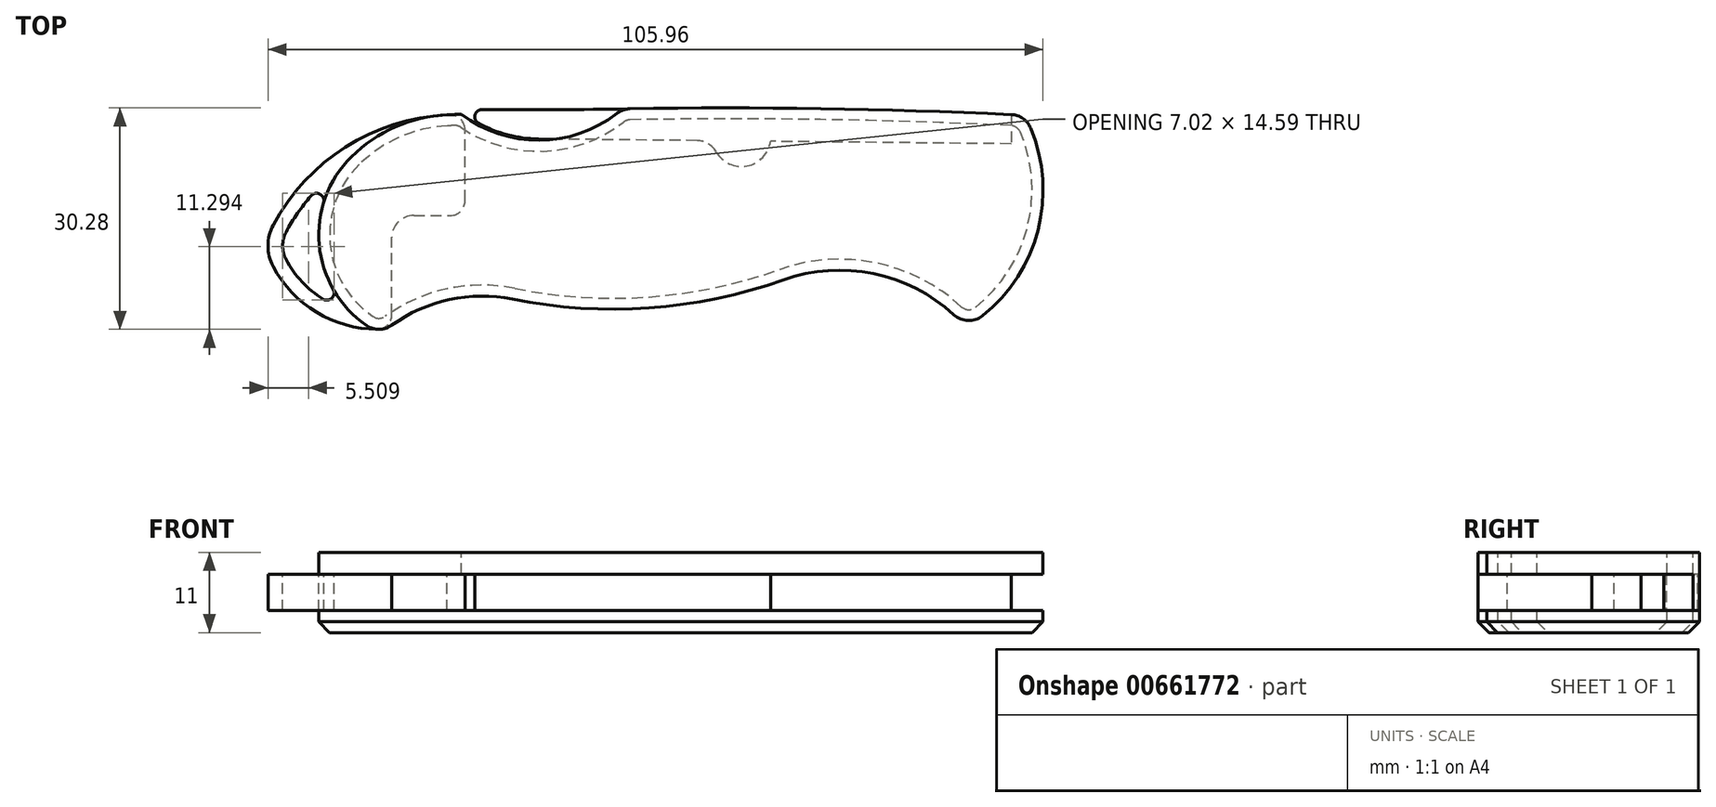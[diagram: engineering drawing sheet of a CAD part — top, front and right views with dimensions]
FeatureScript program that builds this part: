
annotation { "Feature Type Name" : "Feature", "Feature Type Description" : "" }
export const myFeature = defineFeature(function(context is Context, id is Id, definition is map)
    precondition{}
    {
        {
            var Q0;
            Q0=qCreatedBy(makeId("Top.planeOp"),FACE);
            var sketch = newSketch(context, id + "F0", { "sketchPlane" : qUnion([Q0])});
            skLineSegment(sketch, "E0", {"start": v(-50, 0) * mm, "end": v(50, 0) * mm, "construction": true});
            skLineSegment(sketch, "E1", {"start": v(-50, 15) * mm, "end": v(48, 15) * mm});
            skLineSegment(sketch, "E2", {"start": v(48, 15) * mm, "end": v(40, -14) * mm, "construction": true});
            skLineSegment(sketch, "E3", {"start": v(-50, 15) * mm, "end": v(-50, -15) * mm});
            skArc(sketch, "E4", {"start": v(40, -14) * mm, "mid": v(49.73, -1.08) * mm, "end": v(48, 15) * mm});
            skLineSegment(sketch, "E5", {"start": v(-50, -15) * mm, "end": v(40, -14) * mm});
            skSolve(sketch);
        }
        {
            var Q0;
            Q0 = qSketchRegion(id + "F0", true);
            extrude(context, id + "F1", {"entities" : qUnion([Q0]), "depth" : 3 * mm, "offsetDistance" : 25 * mm});
        }
        {
            var Q0;
            Q0=makeQuery(id+"F1.opExtrude","CAP_FACE",FACE,{"disambiguationData":[OSD([sQuery(id+"F0.wireOp",EDGE,"E1"),sQuery(id+"F0.wireOp",EDGE,"E3"),sQuery(id+"F0.wireOp",EDGE,"i1TKLzg2-nzSs-Z2fB-SjIf-EBck5CtR53aa"),sQuery(id+"F0.wireOp",EDGE,"E4")])],"isStart":false});
            var sketch = newSketch(context, id + "F2", { "sketchPlane" : qUnion([Q0])});
            skLineSegment(sketch, "E6", {"start": v(-40, -14.89) * mm, "end": v(40, -14) * mm});
            skArc(sketch, "E7", {"start": v(-22, -10.15) * mm, "mid": v(-31.55, -10.43) * mm, "end": v(-40, -14.89) * mm});
            skArc(sketch, "E8", {"start": v(-22, -10.15) * mm, "mid": v(-3.33, -11.36) * mm, "end": v(15, -7.52) * mm});
            skArc(sketch, "E9", {"start": v(40, -14) * mm, "mid": v(28.49, -6.93) * mm, "end": v(15, -7.52) * mm});
            skSolve(sketch);
        }
        {
            var Q0;
            Q0 = qSketchRegion(id + "F2", true);
            extrude(context, id + "F3", {"entities" : qUnion([Q0]), "operationType" : NewBodyOperationType.REMOVE, "endBound" : BoundingType.THROUGH_ALL, "oppositeDirection" : true, "depth" : 25 * mm, "offsetDistance" : 25 * mm});
        }
        {
            var Q0;
            Q0=makeQuery(id+"F1.opExtrude","CAP_FACE",FACE,{"disambiguationData":[OSD([sQuery(id+"F0.wireOp",EDGE,"E1"),sQuery(id+"F0.wireOp",EDGE,"E3"),sQuery(id+"F0.wireOp",EDGE,"E4"),sQuery(id+"F0.wireOp",EDGE,"E5")])],"isStart":false});
            var sketch = newSketch(context, id + "F4", { "sketchPlane" : qUnion([Q0])});
            skArc(sketch, "E10", {"start": v(48, 15) * mm, "mid": v(8, 16) * mm, "end": v(-32, 15) * mm});
            skLineSegment(sketch, "E11", {"start": v(-32, 15) * mm, "end": v(48, 15) * mm});
            skSolve(sketch);
        }
        {
            var Q0;
            Q0 = qSketchRegion(id + "F4", true);
            var Q1;
            Q1=makeQuery(id+"F1.opExtrude","CAP_FACE",FACE,{"disambiguationData":[OSD([sQuery(id+"F0.wireOp",EDGE,"E1"),sQuery(id+"F0.wireOp",EDGE,"E3"),sQuery(id+"F0.wireOp",EDGE,"E4"),sQuery(id+"F0.wireOp",EDGE,"E5")])],"isStart":true});
            extrude(context, id + "F5", {"entities" : qUnion([Q0]), "operationType" : NewBodyOperationType.ADD, "endBound" : BoundingType.UP_TO_SURFACE, "oppositeDirection" : true, "depth" : 25 * mm, "endBoundEntityFace" : qUnion([Q1]), "offsetDistance" : 25 * mm});
        }
        {
            var Q0;
            Q0=makeQuery(id+"F5.boolean.opBoolean","MERGE",FACE,{"derivedFrom":[makeQuery(id+"F1.opExtrude","CAP_FACE",FACE,{"disambiguationData":[OSD([sQuery(id+"F0.wireOp",EDGE,"E1"),sQuery(id+"F0.wireOp",EDGE,"E3"),sQuery(id+"F0.wireOp",EDGE,"E4"),sQuery(id+"F0.wireOp",EDGE,"E5")])],"isStart":false}),makeQuery(id+"F5.opExtrude","CAP_FACE",FACE,{"disambiguationData":[OSD([sQuery(id+"F4.wireOp",EDGE,"E10"),sQuery(id+"F4.wireOp",EDGE,"E11")])],"isStart":true})]});
            var sketch = newSketch(context, id + "F6", { "sketchPlane" : qUnion([Q0])});
            skArc(sketch, "E12", {"start": v(-29, 15.14) * mm, "mid": v(-17.87, 11.58) * mm, "end": v(-7, 15.86) * mm});
            skArc(sketch, "E13.0", {"start": v(-7, 15.86) * mm, "mid": v(-18, 15.58) * mm, "end": v(-29, 15.14) * mm});
            skPoint(sketch, "E14.orphan", {"position": v(-32, 15) * mm});
            skPoint(sketch, "E15.orphan", {"position": v(48, 15) * mm});
            skSolve(sketch);
        }
        {
            var Q0;
            Q0 = qSketchRegion(id + "F6", true);
            extrude(context, id + "F7", {"entities" : qUnion([Q0]), "operationType" : NewBodyOperationType.REMOVE, "endBound" : BoundingType.THROUGH_ALL, "oppositeDirection" : true, "depth" : 25 * mm, "offsetDistance" : 25 * mm});
        }
        {
            var Q0;
            Q0=makeQuery(id+"F1.opExtrude","SWEPT_EDGE",EDGE,{"disambiguationData":[OSD([sQuery(id+"F0.wireOp",EDGE,"E1"),sQuery(id+"F0.wireOp",EDGE,"E3")])]});
            fillet(context, id + "F8", {"entities" : qUnion([Q0]), "radius" : 20 * mm, "tangentPropagation" : true, "allowEdgeOverflow" : false});
        }
        {
            var Q0;
            Q0=makeQuery(id+"F1.opExtrude","SWEPT_EDGE",EDGE,{"disambiguationData":[OSD([sQuery(id+"F0.wireOp",EDGE,"E3"),sQuery(id+"F0.wireOp",EDGE,"E5")])]});
            fillet(context, id + "F9", {"entities" : qUnion([Q0]), "radius" : 15 * mm, "tangentPropagation" : true, "allowEdgeOverflow" : false});
        }
        {
            var Q0;
            {var subQ0=sQuery(id+"F0.wireOp",EDGE,"E4");Q0=makeQuery(id+"F5.boolean.opBoolean","MERGE",EDGE,{"derivedFrom":[makeQuery(id+"F1.opExtrude","SWEPT_EDGE",EDGE,{"disambiguationData":[OSD([sQuery(id+"F0.wireOp",EDGE,"E1"),subQ0])]}),makeQuery(id+"F5.opExtrude","SWEPT_EDGE",EDGE,{"disambiguationData":[OSD([subQ0,sQuery(id+"F4.wireOp",EDGE,"E10"),sQuery(id+"F4.wireOp",EDGE,"E11")])]})]});}
            var Q1;
            {var subQ0=sQuery(id+"F0.wireOp",EDGE,"E4");Q1=makeQuery(id+"F3.boolean.opBoolean","MERGE",EDGE,{"derivedFrom":[makeQuery(id+"F1.opExtrude","SWEPT_EDGE",EDGE,{"disambiguationData":[OSD([subQ0,sQuery(id+"F0.wireOp",EDGE,"E5")])]}),makeQuery(id+"F3.opExtrude","SWEPT_EDGE",EDGE,{"disambiguationData":[OSD([subQ0,sQuery(id+"F2.wireOp",EDGE,"E6"),sQuery(id+"F2.wireOp",EDGE,"E9")])]})]});}
            var Q2;
            Q2=makeQuery(id+"F9.opFillet","BLEND_EDGE",EDGE,{"blendedFrom":[makeQuery(id+"F1.opExtrude","SWEPT_EDGE",EDGE,{"disambiguationData":[OSD([sQuery(id+"F0.wireOp",EDGE,"E3"),sQuery(id+"F0.wireOp",EDGE,"E5")])]}),makeQuery(id+"F3.boolean.opBoolean","COPY",FACE,{"derivedFrom":makeQuery(id+"F3.opExtrude","SWEPT_FACE",FACE,{"disambiguationData":[OSD([sQuery(id+"F2.wireOp",EDGE,"E7")])]})})],"blendedInto":[makeQuery(id+"F3.boolean.opBoolean","COPY",FACE,{"derivedFrom":makeQuery(id+"F3.opExtrude","SWEPT_FACE",FACE,{"disambiguationData":[OSD([sQuery(id+"F2.wireOp",EDGE,"E7")])]})})]});
            var Q3;
            {var subQ0=sQuery(id+"F6.wireOp",EDGE,"E13.0");var subQ1=sQuery(id+"F6.wireOp",EDGE,"E12");var subQ2=sQuery(id+"F4.wireOp",EDGE,"E10");Q3=makeQuery(id+"F7.boolean.opBoolean","COPY",EDGE,{"derivedFrom":makeQuery(id+"F7.opExtrude","SWEPT_EDGE",EDGE,{"disambiguationData":[OSD([subQ2,subQ1,subQ0]),TDD([makeQuery(id+"F6.imprint","INTERSECT",VERTEX,{"disambiguationData":[OD(0.0)],"derivedFrom":[makeQuery(id+"F5.opExtrude","CAP_EDGE",EDGE,{"disambiguationData":[OSD([subQ2])],"isStart":true}),subQ1,subQ0]})])]})});}
            var Q4;
            {var subQ0=sQuery(id+"F6.wireOp",EDGE,"E13.0");var subQ1=sQuery(id+"F6.wireOp",EDGE,"E12");var subQ2=sQuery(id+"F4.wireOp",EDGE,"E10");Q4=makeQuery(id+"F7.boolean.opBoolean","COPY",EDGE,{"derivedFrom":makeQuery(id+"F7.opExtrude","SWEPT_EDGE",EDGE,{"disambiguationData":[OSD([subQ2,subQ1,subQ0]),TDD([makeQuery(id+"F6.imprint","INTERSECT",VERTEX,{"disambiguationData":[OD(1.0)],"derivedFrom":[makeQuery(id+"F5.opExtrude","CAP_EDGE",EDGE,{"disambiguationData":[OSD([subQ2])],"isStart":true}),subQ1,subQ0]})])]})});}
            fillet(context, id + "F10", {"entities" : qUnion([Q0, Q1, Q2, Q3, Q4]), "radius" : 3 * mm, "tangentPropagation" : true, "allowEdgeOverflow" : false});
        }
        {
            var Q0;
            Q0=makeQuery(id+"F5.boolean.opBoolean","MERGE",FACE,{"derivedFrom":[makeQuery(id+"F1.opExtrude","CAP_FACE",FACE,{"disambiguationData":[OSD([sQuery(id+"F0.wireOp",EDGE,"E1"),sQuery(id+"F0.wireOp",EDGE,"E3"),sQuery(id+"F0.wireOp",EDGE,"E4"),sQuery(id+"F0.wireOp",EDGE,"E5")])],"isStart":true}),makeQuery(id+"F5.opExtrude","CAP_FACE",FACE,{"disambiguationData":[OSD([sQuery(id+"F4.wireOp",EDGE,"E10"),sQuery(id+"F4.wireOp",EDGE,"E11")])],"isStart":false})]});
            var sketch = newSketch(context, id + "F11", { "sketchPlane" : qUnion([Q0])});
            skLineSegment(sketch, "E16", {"start": v(-38.52, 13.72) * mm, "end": v(-38.52, -1.28) * mm});
            skLineSegment(sketch, "E17", {"start": v(-38.52, -1.28) * mm, "end": v(-28.52, -1.28) * mm});
            skLineSegment(sketch, "E18", {"start": v(-28.52, -1.28) * mm, "end": v(-28.52, -15.05) * mm});
            skArc(sketch, "E19", {"start": v(-38.52, 13.72) * mm, "mid": v(-39.33, 14.13) * mm, "end": v(-40.23, 14.28) * mm});
            skArc(sketch, "E20", {"start": v(-40.23, 14.28) * mm, "mid": v(-48.7, 12.02) * mm, "end": v(-54.74, 5.67) * mm});
            skArc(sketch, "E21", {"start": v(-54.74, 5.67) * mm, "mid": v(-55.44, 2.87) * mm, "end": v(-54.74, 0.06) * mm});
            skArc(sketch, "E22", {"start": v(-54.74, 0.06) * mm, "mid": v(-44.86, -10.64) * mm, "end": v(-30.97, -15.05) * mm});
            skLineSegment(sketch, "E23", {"start": v(-30.97, -15.05) * mm, "end": v(-28.52, -15.05) * mm});
            skSolve(sketch);
        }
        {
            var Q0;
            Q0 = qSketchRegion(id + "F11", true);
            extrude(context, id + "F12", {"entities" : qUnion([Q0]), "depth" : 5 * mm, "offsetDistance" : 25 * mm});
        }
        {
            var Q0;
            Q0=makeQuery(id+"F12.opExtrude","CAP_FACE",FACE,{"disambiguationData":[OSD([sQuery(id+"F11.wireOp",EDGE,"E16"),sQuery(id+"F11.wireOp",EDGE,"E17"),sQuery(id+"F11.wireOp",EDGE,"E18"),sQuery(id+"F11.wireOp",EDGE,"E19"),sQuery(id+"F11.wireOp",EDGE,"E20"),sQuery(id+"F11.wireOp",EDGE,"E21"),sQuery(id+"F11.wireOp",EDGE,"E22")])],"isStart":true});
            var sketch = newSketch(context, id + "F13", { "sketchPlane" : qUnion([Q0])});
            skArc(sketch, "E24.0", {"start": v(-44.35, -11.73) * mm, "mid": v(-48.5, -2.08) * mm, "end": v(-45.29, 7.93) * mm});
            skArc(sketch, "E25.0", {"start": v(-52.98, -1) * mm, "mid": v(-49.63, 3.9) * mm, "end": v(-45.29, 7.93) * mm});
            skArc(sketch, "E25.1", {"start": v(-52.98, -4.74) * mm, "mid": v(-53.44, -2.87) * mm, "end": v(-52.98, -1) * mm});
            skArc(sketch, "E25.2", {"start": v(-44.35, -11.73) * mm, "mid": v(-49.38, -9.11) * mm, "end": v(-52.98, -4.74) * mm});
            skPoint(sketch, "E26.orphan", {"position": v(-41.96, -13.76) * mm});
            skPoint(sketch, "E27.orphan", {"position": v(-30.97, 15.05) * mm});
            skPoint(sketch, "E28.orphan", {"position": v(-44.04, 9.31) * mm});
            skSolve(sketch);
        }
        {
            var Q0;
            Q0 = qSketchRegion(id + "F13", true);
            extrude(context, id + "F14", {"entities" : qUnion([Q0]), "operationType" : NewBodyOperationType.REMOVE, "endBound" : BoundingType.THROUGH_ALL, "oppositeDirection" : true, "depth" : 25 * mm, "offsetDistance" : 25 * mm});
        }
        {
            var Q0;
            Q0=makeQuery(id+"F14.boolean.opBoolean","COPY",EDGE,{"derivedFrom":makeQuery(id+"F14.opExtrude","SWEPT_EDGE",EDGE,{"disambiguationData":[OSD([sQuery(id+"F13.wireOp",EDGE,"E24.0"),sQuery(id+"F13.wireOp",EDGE,"E25.0")])]})});
            var Q1;
            Q1=makeQuery(id+"F14.boolean.opBoolean","COPY",EDGE,{"derivedFrom":makeQuery(id+"F14.opExtrude","SWEPT_EDGE",EDGE,{"disambiguationData":[OSD([sQuery(id+"F13.wireOp",EDGE,"E24.0"),sQuery(id+"F13.wireOp",EDGE,"E25.2")])]})});
            fillet(context, id + "F15", {"entities" : qUnion([Q0, Q1]), "radius" : 1 * mm, "tangentPropagation" : true, "allowEdgeOverflow" : false});
        }
        {
            var Q0;
            Q0=makeQuery(id+"F12.opExtrude","SWEPT_EDGE",EDGE,{"disambiguationData":[OSD([sQuery(id+"F11.wireOp",EDGE,"E18"),sQuery(id+"F11.wireOp",EDGE,"E22")])]});
            var Q1;
            Q1=makeQuery(id+"F12.opExtrude","SWEPT_EDGE",EDGE,{"disambiguationData":[OSD([sQuery(id+"F11.wireOp",EDGE,"E17"),sQuery(id+"F11.wireOp",EDGE,"E18")])]});
            var Q2;
            Q2=makeQuery(id+"F12.opExtrude","SWEPT_EDGE",EDGE,{"disambiguationData":[OSD([sQuery(id+"F0.wireOp",EDGE,"E1"),sQuery(id+"F0.wireOp",EDGE,"E3"),sQuery(id+"F0.wireOp",EDGE,"E4"),sQuery(id+"F0.wireOp",EDGE,"E5"),sQuery(id+"F2.wireOp",EDGE,"E7"),sQuery(id+"F11.wireOp",EDGE,"E16"),sQuery(id+"F11.wireOp",EDGE,"E19")])]});
            fillet(context, id + "F16", {"entities" : qUnion([Q0, Q1, Q2]), "radius" : 2 * mm, "tangentPropagation" : true, "allowEdgeOverflow" : false});
        }
        {
            var Q0;
            Q0=makeQuery(id+"F12.opExtrude","SWEPT_EDGE",EDGE,{"disambiguationData":[OSD([sQuery(id+"F11.wireOp",EDGE,"E16"),sQuery(id+"F11.wireOp",EDGE,"E17")])]});
            fillet(context, id + "F17", {"entities" : qUnion([Q0]), "radius" : 3 * mm, "tangentPropagation" : true, "allowEdgeOverflow" : false});
        }
        {
            var Q0;
            Q0=makeQuery(id+"F5.boolean.opBoolean","MERGE",FACE,{"derivedFrom":[makeQuery(id+"F1.opExtrude","CAP_FACE",FACE,{"disambiguationData":[OSD([sQuery(id+"F0.wireOp",EDGE,"E1"),sQuery(id+"F0.wireOp",EDGE,"E3"),sQuery(id+"F0.wireOp",EDGE,"E4"),sQuery(id+"F0.wireOp",EDGE,"E5")])],"isStart":true}),makeQuery(id+"F5.opExtrude","CAP_FACE",FACE,{"disambiguationData":[OSD([sQuery(id+"F4.wireOp",EDGE,"E10"),sQuery(id+"F4.wireOp",EDGE,"E11")])],"isStart":false})]});
            var sketch = newSketch(context, id + "F18", { "sketchPlane" : qUnion([Q0])});
            skArc(sketch, "E29.0", {"start": v(-5.95, -15.88) * mm, "mid": v(20.13, -15.9) * mm, "end": v(46.2, -15.09) * mm});
            skArc(sketch, "E30", {"start": v(-29.45, -15.81) * mm, "mid": v(-17.7, -15.76) * mm, "end": v(-5.95, -15.88) * mm});
            skArc(sketch, "E31", {"start": v(-18.47, -11.76) * mm, "mid": v(-24.31, -12.83) * mm, "end": v(-29.45, -15.81) * mm});
            skLineSegment(sketch, "E32", {"start": v(46.2, -15.09) * mm, "end": v(46.16, -11.09) * mm});
            skLineSegment(sketch, "E33", {"start": v(46.16, -11.09) * mm, "end": v(-18.47, -11.76) * mm});
            skSolve(sketch);
        }
        {
            var Q0;
            Q0 = qSketchRegion(id + "F18", true);
            var Q1;
            Q1=makeQuery(id+"F12.opExtrude","CAP_FACE",FACE,{"disambiguationData":[OSD([sQuery(id+"F11.wireOp",EDGE,"E16"),sQuery(id+"F11.wireOp",EDGE,"E17"),sQuery(id+"F11.wireOp",EDGE,"E18"),sQuery(id+"F11.wireOp",EDGE,"E19"),sQuery(id+"F11.wireOp",EDGE,"E20"),sQuery(id+"F11.wireOp",EDGE,"E21"),sQuery(id+"F11.wireOp",EDGE,"E22"),sQuery(id+"F11.wireOp",EDGE,"E23")])],"isStart":false});
            extrude(context, id + "F19", {"entities" : qUnion([Q0]), "endBound" : BoundingType.UP_TO_SURFACE, "depth" : 25 * mm, "endBoundEntityFace" : qUnion([Q1]), "offsetDistance" : 25 * mm});
        }
        {
            var Q0;
            Q0=makeQuery(id+"F19.opExtrude","CAP_FACE",FACE,{"disambiguationData":[OSD([sQuery(id+"F18.wireOp",EDGE,"E29.0"),sQuery(id+"F18.wireOp",EDGE,"E30"),sQuery(id+"F18.wireOp",EDGE,"E31"),sQuery(id+"F18.wireOp",EDGE,"E32"),sQuery(id+"F18.wireOp",EDGE,"E33")])],"isStart":false});
            var sketch = newSketch(context, id + "F20", { "sketchPlane" : qUnion([Q0])});
            skPoint(sketch, "E34", {"position": v(9.3, -12) * mm});
            skLineSegment(sketch, "E35", {"start": v(9.3, -12) * mm, "end": v(49.3, -12) * mm, "construction": true});
            skCircle(sketch, "E36", {"center": v(9.3, -12) * mm, "radius": 2 * mm, "construction": true});
            skCircle(sketch, "E37.0", {"center": v(9.3, -12) * mm, "radius": 4 * mm, "construction": true});
            skLineSegment(sketch, "E38", {"start": v(9.3, -8) * mm, "end": v(9.3, 11.36) * mm, "construction": true});
            skArc(sketch, "E39", {"start": v(13.26, -11.43) * mm, "mid": v(9.26, -8) * mm, "end": v(5.33, -11.51) * mm});
            skLineSegment(sketch, "E40", {"start": v(5.33, -11.51) * mm, "end": v(13.26, -11.43) * mm});
            skSolve(sketch);
        }
        {
            var Q0;
            Q0 = qSketchRegion(id + "F20", true);
            extrude(context, id + "F21", {"entities" : qUnion([Q0]), "operationType" : NewBodyOperationType.ADD, "oppositeDirection" : true, "depth" : 5 * mm, "offsetDistance" : 25 * mm});
        }
        {
            var Q0;
            {var subQ0=sQuery(id+"F20.wireOp",EDGE,"E40");var subQ1=sQuery(id+"F20.wireOp",EDGE,"E39");var subQ2=sQuery(id+"F18.wireOp",EDGE,"E33");Q0=makeQuery(id+"F21.opExtrude","SWEPT_EDGE",EDGE,{"disambiguationData":[OSD([subQ2,subQ1,subQ0]),TDD([makeQuery(id+"F20.imprint","INTERSECT",VERTEX,{"disambiguationData":[OD(1.0)],"derivedFrom":[makeQuery(id+"F19.opExtrude","CAP_EDGE",EDGE,{"disambiguationData":[OSD([subQ2])],"isStart":false}),subQ1,subQ0]})])]});}
            var Q1;
            {var subQ0=sQuery(id+"F20.wireOp",EDGE,"E40");var subQ1=sQuery(id+"F20.wireOp",EDGE,"E39");var subQ2=sQuery(id+"F18.wireOp",EDGE,"E33");Q1=makeQuery(id+"F21.opExtrude","SWEPT_EDGE",EDGE,{"disambiguationData":[OSD([subQ2,subQ1,subQ0]),TDD([makeQuery(id+"F20.imprint","INTERSECT",VERTEX,{"disambiguationData":[OD(0.0)],"derivedFrom":[makeQuery(id+"F19.opExtrude","CAP_EDGE",EDGE,{"disambiguationData":[OSD([subQ2])],"isStart":false}),subQ1,subQ0]})])]});}
            fillet(context, id + "F22", {"entities" : qUnion([Q0, Q1]), "radius" : 3 * mm, "tangentPropagation" : true, "allowEdgeOverflow" : false});
        }
        {
            var Q0;
            Q0=makeQuery(id+"F19.opExtrude","SWEPT_EDGE",EDGE,{"disambiguationData":[OSD([sQuery(id+"F18.wireOp",EDGE,"E30"),sQuery(id+"F18.wireOp",EDGE,"E31")])]});
            fillet(context, id + "F23", {"entities" : qUnion([Q0]), "radius" : 1 * mm, "tangentPropagation" : true, "allowEdgeOverflow" : false});
        }
        {
            var Q0;
            Q0=makeQuery(id+"F12.opExtrude","CAP_FACE",FACE,{"disambiguationData":[OSD([sQuery(id+"F11.wireOp",EDGE,"E16"),sQuery(id+"F11.wireOp",EDGE,"E17"),sQuery(id+"F11.wireOp",EDGE,"E18"),sQuery(id+"F11.wireOp",EDGE,"E19"),sQuery(id+"F11.wireOp",EDGE,"E20"),sQuery(id+"F11.wireOp",EDGE,"E21"),sQuery(id+"F11.wireOp",EDGE,"E22")])],"isStart":false});
            var sketch = newSketch(context, id + "F24", { "sketchPlane" : qUnion([Q0])});
            skArc(sketch, "E41.0.0", {"start": v(-30.97, -15.05) * mm, "mid": v(-30.5, -15.07) * mm, "end": v(-30.05, -15.1) * mm});
            skArc(sketch, "E41.0.1", {"start": v(-30.05, -15.1) * mm, "mid": v(-29.09, -14.99) * mm, "end": v(-28.22, -14.58) * mm});
            skArc(sketch, "E41.0.2", {"start": v(-28.22, -14.58) * mm, "mid": v(-17.87, -11.58) * mm, "end": v(-7.74, -15.25) * mm});
            skArc(sketch, "E41.0.3", {"start": v(-7.74, -15.25) * mm, "mid": v(-6.9, -15.7) * mm, "end": v(-5.95, -15.88) * mm});
            skArc(sketch, "E41.0.4", {"start": v(-5.95, -15.88) * mm, "mid": v(20.13, -15.9) * mm, "end": v(46.2, -15.09) * mm});
            skArc(sketch, "E41.0.5", {"start": v(46.2, -15.09) * mm, "mid": v(47.78, -14.55) * mm, "end": v(48.82, -13.25) * mm});
            skArc(sketch, "E41.0.6", {"start": v(48.82, -13.25) * mm, "mid": v(49.83, 0.7) * mm, "end": v(42.23, 12.44) * mm});
            skArc(sketch, "E41.0.7", {"start": v(42.23, 12.44) * mm, "mid": v(40.25, 13.09) * mm, "end": v(38.33, 12.3) * mm});
            skArc(sketch, "E41.0.8", {"start": v(38.33, 12.3) * mm, "mid": v(27.33, 6.66) * mm, "end": v(15, 7.52) * mm});
            skArc(sketch, "E41.0.9", {"start": v(15, 7.52) * mm, "mid": v(-3.33, 11.36) * mm, "end": v(-22, 10.15) * mm});
            skArc(sketch, "E41.0.10", {"start": v(-22, 10.15) * mm, "mid": v(-30.63, 10.21) * mm, "end": v(-38.52, 13.72) * mm});
            skArc(sketch, "E41.0.11", {"start": v(-38.52, 13.72) * mm, "mid": v(-40.23, 14.28) * mm, "end": v(-41.96, 13.76) * mm});
            skArc(sketch, "E41.0.12", {"start": v(-41.96, 13.76) * mm, "mid": v(-48.45, 2.71) * mm, "end": v(-44.04, -9.31) * mm});
            skArc(sketch, "E41.0.13", {"start": v(-44.04, -9.31) * mm, "mid": v(-38.04, -13.39) * mm, "end": v(-30.97, -15.05) * mm});
            skSolve(sketch);
        }
        {
            var Q0;
            Q0 = qSketchRegion(id + "F24", true);
            extrude(context, id + "F25", {"entities" : qUnion([Q0]), "depth" : 3 * mm, "offsetDistance" : 25 * mm});
        }
        {
            var Q0;
            Q0=makeQuery(id+"F3.boolean.opBoolean","COPY",EDGE,{"derivedFrom":makeQuery(id+"F3.opExtrude","CAP_EDGE",EDGE,{"disambiguationData":[OSD([sQuery(id+"F2.wireOp",EDGE,"E8")])],"isStart":true})});
            var Q1;
            Q1=makeQuery(id+"F25.opExtrude","CAP_EDGE",EDGE,{"disambiguationData":[OSD([sQuery(id+"F24.wireOp",EDGE,"E41.0.9")])],"isStart":false});
            chamfer(context, id + "F26", {"entities" : qUnion([Q0, Q1]), "width" : 1.5 * mm, "tangentPropagation" : true});
        }
    });
